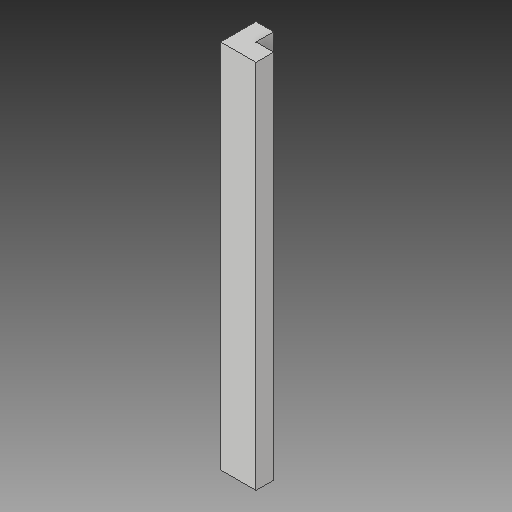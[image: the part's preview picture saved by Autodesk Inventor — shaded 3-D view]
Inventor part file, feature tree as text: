
AUTODESK INVENTOR PART (.ipt)
format: ipt  version: 2017 (Build 210142000, 142)  size: 80,896 bytes
history: native  units: in
note: dims shown in document units (in); Inventor stores cm internally (conversion verified against a paired STEP export)
features: other x3, sketch x3
ambient origin geometry x8: Origin, YZ Plane, XZ Plane, XY Plane, X Axis, Y Axis, Z Axis, Center Point
bodies: Solid1 (feature_tree)
feature tree (6):
  other  "rev1 corners_MIR.ipt"
  other  "Solid1::rev1 corners_MIR.ipt"
  other  "TaggingFeature1"
  sketch  "Sketch1"  dims[d0=0.3937in]
  sketch  "Sketch2"
  sketch  "Sketch3"
